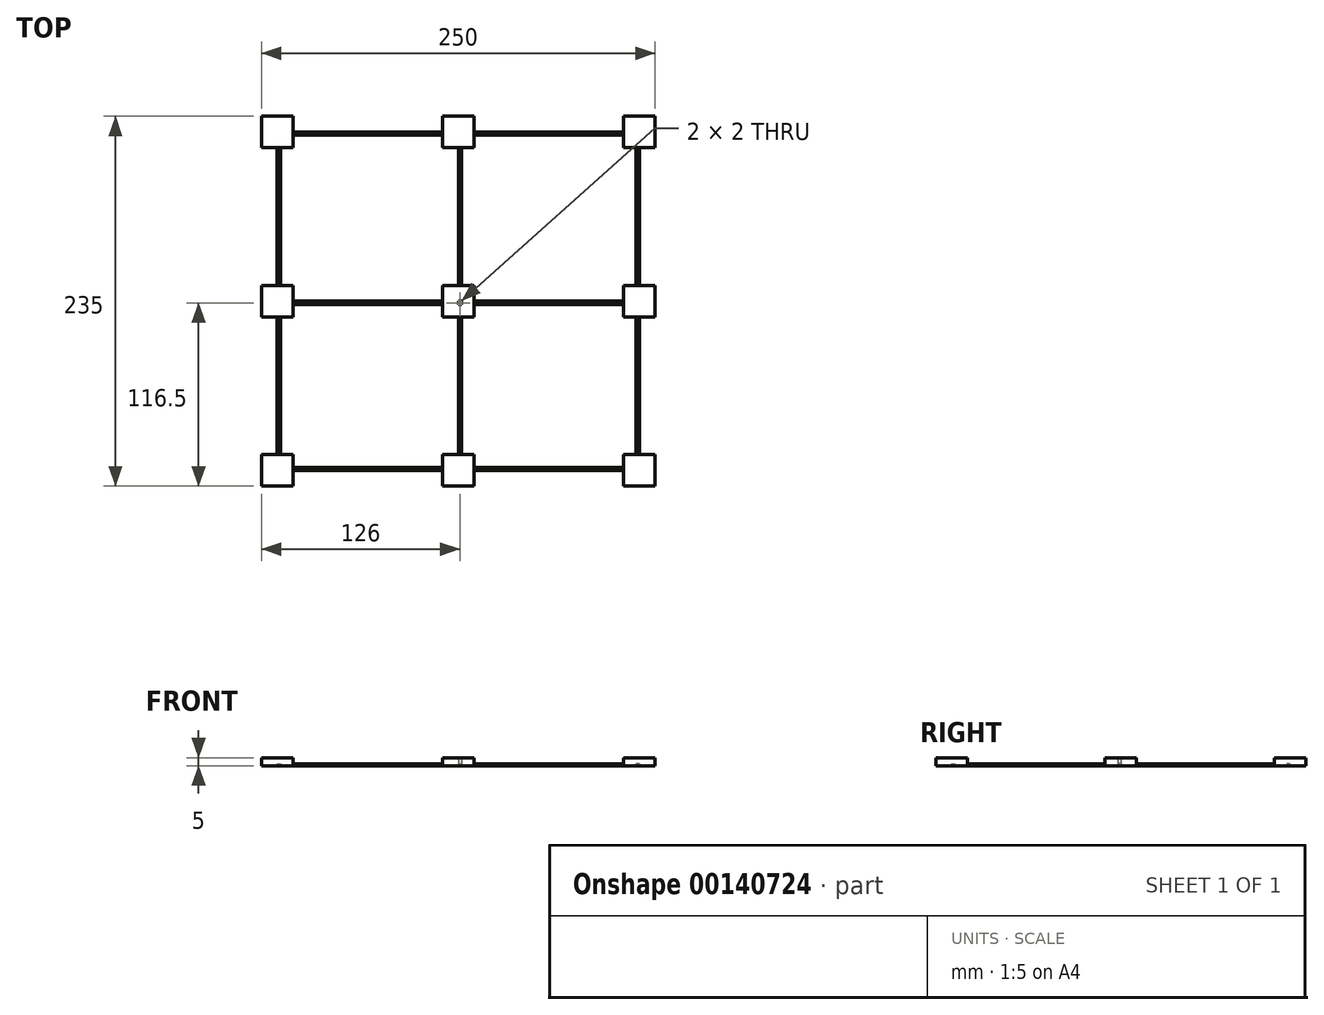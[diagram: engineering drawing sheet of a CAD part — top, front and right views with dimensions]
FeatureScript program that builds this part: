
annotation { "Feature Type Name" : "Feature", "Feature Type Description" : "" }
export const myFeature = defineFeature(function(context is Context, id is Id, definition is map)
    precondition{}
    {
        {
            assignVariable(context, id + "F0", {"name" : "padHeight", "anyValue" : 5});
        }
        {
            assignVariable(context, id + "F1", {"name" : "lineHeight", "anyValue" : 1});
        }
        {
            var Q0;
            Q0=qCreatedBy(makeId("Top.planeOp"),FACE);
            var sketch = newSketch(context, id + "F2", { "sketchPlane" : qUnion([Q0])});
            skLineSegment(sketch, "E0.bottom", {"start": v(125, 117.5) * mm, "end": v(-125, 117.5) * mm, "construction": true});
            skLineSegment(sketch, "E0.top", {"start": v(125, -117.5) * mm, "end": v(-125, -117.5) * mm, "construction": true});
            skLineSegment(sketch, "E0.left", {"start": v(125, 117.5) * mm, "end": v(125, -117.5) * mm, "construction": true});
            skLineSegment(sketch, "E0.right", {"start": v(-125, 117.5) * mm, "end": v(-125, -117.5) * mm, "construction": true});
            skPoint(sketch, "E0.middle", {"position": v(0, 0) * mm});
            skLineSegment(sketch, "E1.bottom", {"start": v(-125, 117.5) * mm, "end": v(-105, 117.5) * mm});
            skLineSegment(sketch, "E1.top", {"start": v(-125, 97.5) * mm, "end": v(-105, 97.5) * mm});
            skLineSegment(sketch, "E1.left", {"start": v(-125, 117.5) * mm, "end": v(-125, 97.5) * mm});
            skLineSegment(sketch, "E1.right", {"start": v(-105, 117.5) * mm, "end": v(-105, 97.5) * mm});
            skLineSegment(sketch, "E2.bottom", {"start": v(125, 117.5) * mm, "end": v(105, 117.5) * mm});
            skLineSegment(sketch, "E2.top", {"start": v(125, 97.5) * mm, "end": v(105, 97.5) * mm});
            skLineSegment(sketch, "E2.left", {"start": v(125, 117.5) * mm, "end": v(125, 97.5) * mm});
            skLineSegment(sketch, "E2.right", {"start": v(105, 117.5) * mm, "end": v(105, 97.5) * mm});
            skLineSegment(sketch, "E3.bottom", {"start": v(125, -117.5) * mm, "end": v(105, -117.5) * mm});
            skLineSegment(sketch, "E3.top", {"start": v(125, -97.5) * mm, "end": v(105, -97.5) * mm});
            skLineSegment(sketch, "E3.left", {"start": v(125, -117.5) * mm, "end": v(125, -97.5) * mm});
            skLineSegment(sketch, "E3.right", {"start": v(105, -117.5) * mm, "end": v(105, -97.5) * mm});
            skLineSegment(sketch, "E4.bottom", {"start": v(-125, -117.5) * mm, "end": v(-105, -117.5) * mm});
            skLineSegment(sketch, "E4.top", {"start": v(-125, -97.5) * mm, "end": v(-105, -97.5) * mm});
            skLineSegment(sketch, "E4.left", {"start": v(-125, -117.5) * mm, "end": v(-125, -97.5) * mm});
            skLineSegment(sketch, "E4.right", {"start": v(-105, -117.5) * mm, "end": v(-105, -97.5) * mm});
            skLineSegment(sketch, "E5.bottom", {"start": v(-10, 10) * mm, "end": v(10, 10) * mm});
            skLineSegment(sketch, "E5.top", {"start": v(-10, -10) * mm, "end": v(10, -10) * mm});
            skLineSegment(sketch, "E5.left", {"start": v(-10, 10) * mm, "end": v(-10, -10) * mm});
            skLineSegment(sketch, "E5.right", {"start": v(10, 10) * mm, "end": v(10, -10) * mm});
            skLineSegment(sketch, "E6.bottom", {"start": v(125, 10) * mm, "end": v(105, 10) * mm});
            skLineSegment(sketch, "E6.top", {"start": v(125, -10) * mm, "end": v(105, -10) * mm});
            skLineSegment(sketch, "E6.left", {"start": v(125, 10) * mm, "end": v(125, -10) * mm});
            skLineSegment(sketch, "E6.right", {"start": v(105, 10) * mm, "end": v(105, -10) * mm});
            skLineSegment(sketch, "E7.bottom", {"start": v(-125, 10) * mm, "end": v(-105, 10) * mm});
            skLineSegment(sketch, "E7.top", {"start": v(-125, -10) * mm, "end": v(-105, -10) * mm});
            skLineSegment(sketch, "E7.left", {"start": v(-125, 10) * mm, "end": v(-125, -10) * mm});
            skLineSegment(sketch, "E7.right", {"start": v(-105, 10) * mm, "end": v(-105, -10) * mm});
            skLineSegment(sketch, "E8.bottom", {"start": v(-10, 117.5) * mm, "end": v(10, 117.5) * mm});
            skLineSegment(sketch, "E8.top", {"start": v(-10, 97.5) * mm, "end": v(10, 97.5) * mm});
            skLineSegment(sketch, "E8.left", {"start": v(-10, 117.5) * mm, "end": v(-10, 97.5) * mm});
            skLineSegment(sketch, "E8.right", {"start": v(10, 117.5) * mm, "end": v(10, 97.5) * mm});
            skLineSegment(sketch, "E9.bottom", {"start": v(10, -117.5) * mm, "end": v(-10, -117.5) * mm});
            skLineSegment(sketch, "E9.top", {"start": v(10, -97.5) * mm, "end": v(-10, -97.5) * mm});
            skLineSegment(sketch, "E9.left", {"start": v(10, -117.5) * mm, "end": v(10, -97.5) * mm});
            skLineSegment(sketch, "E9.right", {"start": v(-10, -117.5) * mm, "end": v(-10, -97.5) * mm});
            skLineSegment(sketch, "E10.bottom", {"start": v(-115, 107.5) * mm, "end": v(115, 107.5) * mm});
            skLineSegment(sketch, "E10.top", {"start": v(-115, -107.5) * mm, "end": v(115, -107.5) * mm});
            skLineSegment(sketch, "E10.left", {"start": v(-115, 107.5) * mm, "end": v(-115, -107.5) * mm});
            skLineSegment(sketch, "E10.right", {"start": v(115, 107.5) * mm, "end": v(115, -107.5) * mm});
            skPoint(sketch, "E10.cornerSnap0", {"position": v(-105, 107.5) * mm});
            skPoint(sketch, "E10.cornerSnap1", {"position": v(-115, 97.5) * mm});
            skLineSegment(sketch, "E11.bottom", {"start": v(-113, 105.5) * mm, "end": v(113, 105.5) * mm});
            skLineSegment(sketch, "E11.top", {"start": v(-113, -105.5) * mm, "end": v(113, -105.5) * mm});
            skLineSegment(sketch, "E11.left", {"start": v(-113, 105.5) * mm, "end": v(-113, -105.5) * mm});
            skLineSegment(sketch, "E11.right", {"start": v(113, 105.5) * mm, "end": v(113, -105.5) * mm});
            skLineSegment(sketch, "E12", {"start": v(0, 97.5) * mm, "end": v(0, -97.5) * mm});
            skLineSegment(sketch, "E13", {"start": v(2, 97.5) * mm, "end": v(2, -97.5) * mm});
            skLineSegment(sketch, "E14", {"start": v(-105, 0) * mm, "end": v(105, 0) * mm});
            skLineSegment(sketch, "E15", {"start": v(-105, -2) * mm, "end": v(105, -2) * mm});
            skSolve(sketch);
        }
        {
            var Q0;
            {var subQ1=sQuery(id+"F2.wireOp",EDGE,"E1.bottom");Q0=makeQuery(id+"F2.imprint","IMPRINT",FACE,{"disambiguationData":[TD([[makeQuery(id+"F2.imprint","IMPRINT",EDGE,{"derivedFrom":subQ1}),-1.0]])]});}
            var Q1;
            {var subQ0=sQuery(id+"F2.wireOp",EDGE,"E10.left");var subQ3=sQuery(id+"F2.wireOp",EDGE,"E1.top");var subQ4=makeQuery(id+"F2.imprint","INTERSECT",VERTEX,{"derivedFrom":[subQ3,subQ0]});Q1=makeQuery(id+"F2.imprint","IMPRINT",FACE,{"disambiguationData":[TD([[makeQuery(id+"F2.imprint","IMPRINT",EDGE,{"disambiguationData":[TD([[subQ4,-1.0]])],"derivedFrom":subQ3}),1.0]])]});}
            var Q2;
            {var subQ0=sQuery(id+"F2.wireOp",EDGE,"E1.right");var subQ1=sQuery(id+"F2.wireOp",EDGE,"E1.top");var subQ2=makeQuery(id+"F2.imprint","INTERSECT",VERTEX,{"derivedFrom":[subQ1,subQ0]});Q2=makeQuery(id+"F2.imprint","IMPRINT",FACE,{"disambiguationData":[TD([[makeQuery(id+"F2.imprint","IMPRINT",EDGE,{"disambiguationData":[TD([[subQ2,1.0]])],"derivedFrom":subQ1}),1.0]])]});}
            var Q3;
            {var subQ0=sQuery(id+"F2.wireOp",EDGE,"E8.bottom");Q3=makeQuery(id+"F2.imprint","IMPRINT",FACE,{"disambiguationData":[TD([[makeQuery(id+"F2.imprint","IMPRINT",EDGE,{"derivedFrom":subQ0}),-1.0]])]});}
            var Q4;
            {var subQ0=sQuery(id+"F2.wireOp",EDGE,"E10.bottom");var subQ1=sQuery(id+"F2.wireOp",EDGE,"E8.left");var subQ2=makeQuery(id+"F2.imprint","INTERSECT",VERTEX,{"derivedFrom":[subQ1,subQ0]});Q4=makeQuery(id+"F2.imprint","IMPRINT",FACE,{"disambiguationData":[TD([[makeQuery(id+"F2.imprint","IMPRINT",EDGE,{"disambiguationData":[TD([[subQ2,-1.0]])],"derivedFrom":subQ1}),1.0]])]});}
            var Q5;
            {var subQ0=sQuery(id+"F2.wireOp",EDGE,"E8.left");var subQ1=sQuery(id+"F2.wireOp",EDGE,"E8.top");var subQ2=makeQuery(id+"F2.imprint","INTERSECT",VERTEX,{"derivedFrom":[subQ1,subQ0]});Q5=makeQuery(id+"F2.imprint","IMPRINT",FACE,{"disambiguationData":[TD([[makeQuery(id+"F2.imprint","IMPRINT",EDGE,{"disambiguationData":[TD([[subQ2,-1.0]])],"derivedFrom":subQ1}),1.0]])]});}
            var Q6;
            {var subQ1=sQuery(id+"F2.wireOp",EDGE,"E2.bottom");Q6=makeQuery(id+"F2.imprint","IMPRINT",FACE,{"disambiguationData":[TD([[makeQuery(id+"F2.imprint","IMPRINT",EDGE,{"derivedFrom":subQ1}),1.0]])]});}
            var Q7;
            {var subQ0=sQuery(id+"F2.wireOp",EDGE,"E10.right");var subQ3=sQuery(id+"F2.wireOp",EDGE,"E2.top");var subQ4=makeQuery(id+"F2.imprint","INTERSECT",VERTEX,{"derivedFrom":[subQ3,subQ0]});Q7=makeQuery(id+"F2.imprint","IMPRINT",FACE,{"disambiguationData":[TD([[makeQuery(id+"F2.imprint","IMPRINT",EDGE,{"disambiguationData":[TD([[subQ4,-1.0]])],"derivedFrom":subQ3}),-1.0]])]});}
            var Q8;
            {var subQ0=sQuery(id+"F2.wireOp",EDGE,"E2.right");var subQ1=sQuery(id+"F2.wireOp",EDGE,"E2.top");var subQ2=makeQuery(id+"F2.imprint","INTERSECT",VERTEX,{"derivedFrom":[subQ1,subQ0]});Q8=makeQuery(id+"F2.imprint","IMPRINT",FACE,{"disambiguationData":[TD([[makeQuery(id+"F2.imprint","IMPRINT",EDGE,{"disambiguationData":[TD([[subQ2,1.0]])],"derivedFrom":subQ1}),-1.0]])]});}
            var Q9;
            {var subQ0=sQuery(id+"F2.wireOp",EDGE,"E7.left");Q9=makeQuery(id+"F2.imprint","IMPRINT",FACE,{"disambiguationData":[TD([[makeQuery(id+"F2.imprint","IMPRINT",EDGE,{"derivedFrom":subQ0}),1.0]])]});}
            var Q10;
            {var subQ0=sQuery(id+"F2.wireOp",EDGE,"E10.left");var subQ1=sQuery(id+"F2.wireOp",EDGE,"E7.bottom");var subQ2=makeQuery(id+"F2.imprint","INTERSECT",VERTEX,{"derivedFrom":[subQ1,subQ0]});Q10=makeQuery(id+"F2.imprint","IMPRINT",FACE,{"disambiguationData":[TD([[makeQuery(id+"F2.imprint","IMPRINT",EDGE,{"disambiguationData":[TD([[subQ2,-1.0]])],"derivedFrom":subQ1}),-1.0]])]});}
            var Q11;
            {var subQ0=sQuery(id+"F2.wireOp",EDGE,"E7.right");var subQ3=sQuery(id+"F2.wireOp",EDGE,"E7.bottom");var subQ4=makeQuery(id+"F2.imprint","INTERSECT",VERTEX,{"derivedFrom":[subQ3,subQ0]});Q11=makeQuery(id+"F2.imprint","IMPRINT",FACE,{"disambiguationData":[TD([[makeQuery(id+"F2.imprint","IMPRINT",EDGE,{"disambiguationData":[TD([[subQ4,1.0]])],"derivedFrom":subQ3}),-1.0]])]});}
            var Q12;
            {var subQ0=sQuery(id+"F2.wireOp",EDGE,"E5.left");var subQ1=sQuery(id+"F2.wireOp",EDGE,"E5.top");var subQ2=makeQuery(id+"F2.imprint","INTERSECT",VERTEX,{"derivedFrom":[subQ1,subQ0]});Q12=makeQuery(id+"F2.imprint","IMPRINT",FACE,{"disambiguationData":[TD([[makeQuery(id+"F2.imprint","IMPRINT",EDGE,{"disambiguationData":[TD([[subQ2,-1.0]])],"derivedFrom":subQ1}),1.0]])]});}
            var Q13;
            {var subQ0=sQuery(id+"F2.wireOp",EDGE,"E14");var subQ1=sQuery(id+"F2.wireOp",EDGE,"E5.left");var subQ2=makeQuery(id+"F2.imprint","INTERSECT",VERTEX,{"derivedFrom":[subQ1,subQ0]});Q13=makeQuery(id+"F2.imprint","IMPRINT",FACE,{"disambiguationData":[TD([[makeQuery(id+"F2.imprint","IMPRINT",EDGE,{"disambiguationData":[TD([[subQ2,-1.0]])],"derivedFrom":subQ1}),1.0]])]});}
            var Q14;
            {var subQ0=sQuery(id+"F2.wireOp",EDGE,"E5.left");var subQ1=sQuery(id+"F2.wireOp",EDGE,"E5.bottom");var subQ2=makeQuery(id+"F2.imprint","INTERSECT",VERTEX,{"derivedFrom":[subQ1,subQ0]});Q14=makeQuery(id+"F2.imprint","IMPRINT",FACE,{"disambiguationData":[TD([[makeQuery(id+"F2.imprint","IMPRINT",EDGE,{"disambiguationData":[TD([[subQ2,-1.0]])],"derivedFrom":subQ1}),-1.0]])]});}
            var Q15;
            {var subQ0=sQuery(id+"F2.wireOp",EDGE,"E5.right");var subQ1=sQuery(id+"F2.wireOp",EDGE,"E5.bottom");var subQ2=makeQuery(id+"F2.imprint","INTERSECT",VERTEX,{"derivedFrom":[subQ1,subQ0]});Q15=makeQuery(id+"F2.imprint","IMPRINT",FACE,{"disambiguationData":[TD([[makeQuery(id+"F2.imprint","IMPRINT",EDGE,{"disambiguationData":[TD([[subQ2,1.0]])],"derivedFrom":subQ1}),-1.0]])]});}
            var Q16;
            {var subQ0=sQuery(id+"F2.wireOp",EDGE,"E12");var subQ1=sQuery(id+"F2.wireOp",EDGE,"E5.bottom");var subQ2=makeQuery(id+"F2.imprint","INTERSECT",VERTEX,{"derivedFrom":[subQ1,subQ0]});Q16=makeQuery(id+"F2.imprint","IMPRINT",FACE,{"disambiguationData":[TD([[makeQuery(id+"F2.imprint","IMPRINT",EDGE,{"disambiguationData":[TD([[subQ2,-1.0]])],"derivedFrom":subQ1}),-1.0]])]});}
            var Q17;
            {var subQ0=sQuery(id+"F2.wireOp",EDGE,"E12");var subQ1=sQuery(id+"F2.wireOp",EDGE,"E5.top");var subQ2=makeQuery(id+"F2.imprint","INTERSECT",VERTEX,{"derivedFrom":[subQ1,subQ0]});Q17=makeQuery(id+"F2.imprint","IMPRINT",FACE,{"disambiguationData":[TD([[makeQuery(id+"F2.imprint","IMPRINT",EDGE,{"disambiguationData":[TD([[subQ2,-1.0]])],"derivedFrom":subQ1}),1.0]])]});}
            var Q18;
            {var subQ0=sQuery(id+"F2.wireOp",EDGE,"E5.right");var subQ1=sQuery(id+"F2.wireOp",EDGE,"E5.top");var subQ2=makeQuery(id+"F2.imprint","INTERSECT",VERTEX,{"derivedFrom":[subQ1,subQ0]});Q18=makeQuery(id+"F2.imprint","IMPRINT",FACE,{"disambiguationData":[TD([[makeQuery(id+"F2.imprint","IMPRINT",EDGE,{"disambiguationData":[TD([[subQ2,1.0]])],"derivedFrom":subQ1}),1.0]])]});}
            var Q19;
            {var subQ0=sQuery(id+"F2.wireOp",EDGE,"E14");var subQ1=sQuery(id+"F2.wireOp",EDGE,"E5.right");var subQ2=makeQuery(id+"F2.imprint","INTERSECT",VERTEX,{"derivedFrom":[subQ1,subQ0]});Q19=makeQuery(id+"F2.imprint","IMPRINT",FACE,{"disambiguationData":[TD([[makeQuery(id+"F2.imprint","IMPRINT",EDGE,{"disambiguationData":[TD([[subQ2,-1.0]])],"derivedFrom":subQ1}),-1.0]])]});}
            var Q20;
            {var subQ0=sQuery(id+"F2.wireOp",EDGE,"E6.right");var subQ3=sQuery(id+"F2.wireOp",EDGE,"E6.bottom");var subQ4=makeQuery(id+"F2.imprint","INTERSECT",VERTEX,{"derivedFrom":[subQ3,subQ0]});Q20=makeQuery(id+"F2.imprint","IMPRINT",FACE,{"disambiguationData":[TD([[makeQuery(id+"F2.imprint","IMPRINT",EDGE,{"disambiguationData":[TD([[subQ4,1.0]])],"derivedFrom":subQ3}),1.0]])]});}
            var Q21;
            {var subQ0=sQuery(id+"F2.wireOp",EDGE,"E10.right");var subQ1=sQuery(id+"F2.wireOp",EDGE,"E6.bottom");var subQ2=makeQuery(id+"F2.imprint","INTERSECT",VERTEX,{"derivedFrom":[subQ1,subQ0]});Q21=makeQuery(id+"F2.imprint","IMPRINT",FACE,{"disambiguationData":[TD([[makeQuery(id+"F2.imprint","IMPRINT",EDGE,{"disambiguationData":[TD([[subQ2,-1.0]])],"derivedFrom":subQ1}),1.0]])]});}
            var Q22;
            {var subQ0=sQuery(id+"F2.wireOp",EDGE,"E6.left");Q22=makeQuery(id+"F2.imprint","IMPRINT",FACE,{"disambiguationData":[TD([[makeQuery(id+"F2.imprint","IMPRINT",EDGE,{"derivedFrom":subQ0}),-1.0]])]});}
            var Q23;
            {var subQ1=sQuery(id+"F2.wireOp",EDGE,"E4.bottom");Q23=makeQuery(id+"F2.imprint","IMPRINT",FACE,{"disambiguationData":[TD([[makeQuery(id+"F2.imprint","IMPRINT",EDGE,{"derivedFrom":subQ1}),1.0]])]});}
            var Q24;
            {var subQ0=sQuery(id+"F2.wireOp",EDGE,"E10.left");var subQ3=sQuery(id+"F2.wireOp",EDGE,"E4.top");var subQ4=makeQuery(id+"F2.imprint","INTERSECT",VERTEX,{"derivedFrom":[subQ3,subQ0]});Q24=makeQuery(id+"F2.imprint","IMPRINT",FACE,{"disambiguationData":[TD([[makeQuery(id+"F2.imprint","IMPRINT",EDGE,{"disambiguationData":[TD([[subQ4,-1.0]])],"derivedFrom":subQ3}),-1.0]])]});}
            var Q25;
            {var subQ0=sQuery(id+"F2.wireOp",EDGE,"E4.right");var subQ1=sQuery(id+"F2.wireOp",EDGE,"E4.top");var subQ2=makeQuery(id+"F2.imprint","INTERSECT",VERTEX,{"derivedFrom":[subQ1,subQ0]});Q25=makeQuery(id+"F2.imprint","IMPRINT",FACE,{"disambiguationData":[TD([[makeQuery(id+"F2.imprint","IMPRINT",EDGE,{"disambiguationData":[TD([[subQ2,1.0]])],"derivedFrom":subQ1}),-1.0]])]});}
            var Q26;
            {var subQ0=sQuery(id+"F2.wireOp",EDGE,"E9.bottom");Q26=makeQuery(id+"F2.imprint","IMPRINT",FACE,{"disambiguationData":[TD([[makeQuery(id+"F2.imprint","IMPRINT",EDGE,{"derivedFrom":subQ0}),-1.0]])]});}
            var Q27;
            {var subQ0=sQuery(id+"F2.wireOp",EDGE,"E10.top");var subQ1=sQuery(id+"F2.wireOp",EDGE,"E9.left");var subQ2=makeQuery(id+"F2.imprint","INTERSECT",VERTEX,{"derivedFrom":[subQ1,subQ0]});Q27=makeQuery(id+"F2.imprint","IMPRINT",FACE,{"disambiguationData":[TD([[makeQuery(id+"F2.imprint","IMPRINT",EDGE,{"disambiguationData":[TD([[subQ2,-1.0]])],"derivedFrom":subQ1}),1.0]])]});}
            var Q28;
            {var subQ0=sQuery(id+"F2.wireOp",EDGE,"E9.left");var subQ1=sQuery(id+"F2.wireOp",EDGE,"E9.top");var subQ2=makeQuery(id+"F2.imprint","INTERSECT",VERTEX,{"derivedFrom":[subQ1,subQ0]});Q28=makeQuery(id+"F2.imprint","IMPRINT",FACE,{"disambiguationData":[TD([[makeQuery(id+"F2.imprint","IMPRINT",EDGE,{"disambiguationData":[TD([[subQ2,-1.0]])],"derivedFrom":subQ1}),1.0]])]});}
            var Q29;
            {var subQ1=sQuery(id+"F2.wireOp",EDGE,"E3.bottom");Q29=makeQuery(id+"F2.imprint","IMPRINT",FACE,{"disambiguationData":[TD([[makeQuery(id+"F2.imprint","IMPRINT",EDGE,{"derivedFrom":subQ1}),-1.0]])]});}
            var Q30;
            {var subQ0=sQuery(id+"F2.wireOp",EDGE,"E10.right");var subQ5=sQuery(id+"F2.wireOp",EDGE,"E3.top");var subQ6=makeQuery(id+"F2.imprint","INTERSECT",VERTEX,{"derivedFrom":[subQ5,subQ0]});Q30=makeQuery(id+"F2.imprint","IMPRINT",FACE,{"disambiguationData":[TD([[makeQuery(id+"F2.imprint","IMPRINT",EDGE,{"disambiguationData":[TD([[subQ6,-1.0]])],"derivedFrom":subQ5}),1.0]])]});}
            var Q31;
            {var subQ0=sQuery(id+"F2.wireOp",EDGE,"E3.right");var subQ1=sQuery(id+"F2.wireOp",EDGE,"E3.top");var subQ2=makeQuery(id+"F2.imprint","INTERSECT",VERTEX,{"derivedFrom":[subQ1,subQ0]});Q31=makeQuery(id+"F2.imprint","IMPRINT",FACE,{"disambiguationData":[TD([[makeQuery(id+"F2.imprint","IMPRINT",EDGE,{"disambiguationData":[TD([[subQ2,1.0]])],"derivedFrom":subQ1}),1.0]])]});}
            extrude(context, id + "F3", {"entities" : qUnion([Q0, Q1, Q2, Q3, Q4, Q5, Q6, Q7, Q8, Q9, Q10, Q11, Q12, Q13, Q14, Q15, Q16, Q17, Q18, Q19, Q20, Q21, Q22, Q23, Q24, Q25, Q26, Q27, Q28, Q29, Q30, Q31]), "depth" : (getVariable(context, 'padHeight')) * mm});
        }
        {
            var Q0;
            {var subQ0=sQuery(id+"F2.wireOp",EDGE,"E10.bottom");var subQ1=sQuery(id+"F2.wireOp",EDGE,"E1.right");var subQ2=makeQuery(id+"F2.imprint","INTERSECT",VERTEX,{"derivedFrom":[subQ1,subQ0]});Q0=makeQuery(id+"F2.imprint","IMPRINT",FACE,{"disambiguationData":[TD([[makeQuery(id+"F2.imprint","IMPRINT",EDGE,{"disambiguationData":[TD([[subQ2,-1.0]])],"derivedFrom":subQ1}),1.0]])]});}
            var Q1;
            {var subQ0=sQuery(id+"F2.wireOp",EDGE,"E10.bottom");var subQ1=sQuery(id+"F2.wireOp",EDGE,"E2.right");var subQ2=makeQuery(id+"F2.imprint","INTERSECT",VERTEX,{"derivedFrom":[subQ1,subQ0]});Q1=makeQuery(id+"F2.imprint","IMPRINT",FACE,{"disambiguationData":[TD([[makeQuery(id+"F2.imprint","IMPRINT",EDGE,{"disambiguationData":[TD([[subQ2,-1.0]])],"derivedFrom":subQ1}),-1.0]])]});}
            var Q2;
            {var subQ0=sQuery(id+"F2.wireOp",EDGE,"E10.right");var subQ1=sQuery(id+"F2.wireOp",EDGE,"E2.top");var subQ2=makeQuery(id+"F2.imprint","INTERSECT",VERTEX,{"derivedFrom":[subQ1,subQ0]});Q2=makeQuery(id+"F2.imprint","IMPRINT",FACE,{"disambiguationData":[TD([[makeQuery(id+"F2.imprint","IMPRINT",EDGE,{"disambiguationData":[TD([[subQ2,-1.0]])],"derivedFrom":subQ1}),1.0]])]});}
            var Q3;
            {var subQ0=sQuery(id+"F2.wireOp",EDGE,"E10.right");var subQ1=sQuery(id+"F2.wireOp",EDGE,"E3.top");var subQ2=makeQuery(id+"F2.imprint","INTERSECT",VERTEX,{"derivedFrom":[subQ1,subQ0]});Q3=makeQuery(id+"F2.imprint","IMPRINT",FACE,{"disambiguationData":[TD([[makeQuery(id+"F2.imprint","IMPRINT",EDGE,{"disambiguationData":[TD([[subQ2,-1.0]])],"derivedFrom":subQ1}),-1.0]])]});}
            var Q4;
            {var subQ0=sQuery(id+"F2.wireOp",EDGE,"E10.top");var subQ1=sQuery(id+"F2.wireOp",EDGE,"E3.right");var subQ2=makeQuery(id+"F2.imprint","INTERSECT",VERTEX,{"derivedFrom":[subQ1,subQ0]});Q4=makeQuery(id+"F2.imprint","IMPRINT",FACE,{"disambiguationData":[TD([[makeQuery(id+"F2.imprint","IMPRINT",EDGE,{"disambiguationData":[TD([[subQ2,-1.0]])],"derivedFrom":subQ1}),1.0]])]});}
            var Q5;
            {var subQ0=sQuery(id+"F2.wireOp",EDGE,"E10.top");var subQ1=sQuery(id+"F2.wireOp",EDGE,"E4.right");var subQ2=makeQuery(id+"F2.imprint","INTERSECT",VERTEX,{"derivedFrom":[subQ1,subQ0]});Q5=makeQuery(id+"F2.imprint","IMPRINT",FACE,{"disambiguationData":[TD([[makeQuery(id+"F2.imprint","IMPRINT",EDGE,{"disambiguationData":[TD([[subQ2,-1.0]])],"derivedFrom":subQ1}),-1.0]])]});}
            var Q6;
            {var subQ0=sQuery(id+"F2.wireOp",EDGE,"E10.left");var subQ1=sQuery(id+"F2.wireOp",EDGE,"E4.top");var subQ2=makeQuery(id+"F2.imprint","INTERSECT",VERTEX,{"derivedFrom":[subQ1,subQ0]});Q6=makeQuery(id+"F2.imprint","IMPRINT",FACE,{"disambiguationData":[TD([[makeQuery(id+"F2.imprint","IMPRINT",EDGE,{"disambiguationData":[TD([[subQ2,-1.0]])],"derivedFrom":subQ1}),1.0]])]});}
            var Q7;
            {var subQ0=sQuery(id+"F2.wireOp",EDGE,"E10.left");var subQ1=sQuery(id+"F2.wireOp",EDGE,"E1.top");var subQ2=makeQuery(id+"F2.imprint","INTERSECT",VERTEX,{"derivedFrom":[subQ1,subQ0]});Q7=makeQuery(id+"F2.imprint","IMPRINT",FACE,{"disambiguationData":[TD([[makeQuery(id+"F2.imprint","IMPRINT",EDGE,{"disambiguationData":[TD([[subQ2,-1.0]])],"derivedFrom":subQ1}),-1.0]])]});}
            var Q8;
            {var subQ0=sQuery(id+"F2.wireOp",EDGE,"E12");var subQ1=sQuery(id+"F2.wireOp",EDGE,"E5.bottom");var subQ2=makeQuery(id+"F2.imprint","INTERSECT",VERTEX,{"derivedFrom":[subQ1,subQ0]});Q8=makeQuery(id+"F2.imprint","IMPRINT",FACE,{"disambiguationData":[TD([[makeQuery(id+"F2.imprint","IMPRINT",EDGE,{"disambiguationData":[TD([[subQ2,-1.0]])],"derivedFrom":subQ1}),1.0]])]});}
            var Q9;
            {var subQ0=sQuery(id+"F2.wireOp",EDGE,"E12");var subQ1=sQuery(id+"F2.wireOp",EDGE,"E5.top");var subQ2=makeQuery(id+"F2.imprint","INTERSECT",VERTEX,{"derivedFrom":[subQ1,subQ0]});Q9=makeQuery(id+"F2.imprint","IMPRINT",FACE,{"disambiguationData":[TD([[makeQuery(id+"F2.imprint","IMPRINT",EDGE,{"disambiguationData":[TD([[subQ2,-1.0]])],"derivedFrom":subQ1}),-1.0]])]});}
            var Q10;
            {var subQ0=sQuery(id+"F2.wireOp",EDGE,"E14");var subQ1=sQuery(id+"F2.wireOp",EDGE,"E5.left");var subQ2=makeQuery(id+"F2.imprint","INTERSECT",VERTEX,{"derivedFrom":[subQ1,subQ0]});Q10=makeQuery(id+"F2.imprint","IMPRINT",FACE,{"disambiguationData":[TD([[makeQuery(id+"F2.imprint","IMPRINT",EDGE,{"disambiguationData":[TD([[subQ2,-1.0]])],"derivedFrom":subQ1}),-1.0]])]});}
            var Q11;
            {var subQ0=sQuery(id+"F2.wireOp",EDGE,"E14");var subQ1=sQuery(id+"F2.wireOp",EDGE,"E5.right");var subQ2=makeQuery(id+"F2.imprint","INTERSECT",VERTEX,{"derivedFrom":[subQ1,subQ0]});Q11=makeQuery(id+"F2.imprint","IMPRINT",FACE,{"disambiguationData":[TD([[makeQuery(id+"F2.imprint","IMPRINT",EDGE,{"disambiguationData":[TD([[subQ2,-1.0]])],"derivedFrom":subQ1}),1.0]])]});}
            extrude(context, id + "F4", {"entities" : qUnion([Q0, Q1, Q2, Q3, Q4, Q5, Q6, Q7, Q8, Q9, Q10, Q11]), "operationType" : NewBodyOperationType.ADD, "depth" : (getVariable(context, 'lineHeight')) * mm});
        }
    });
